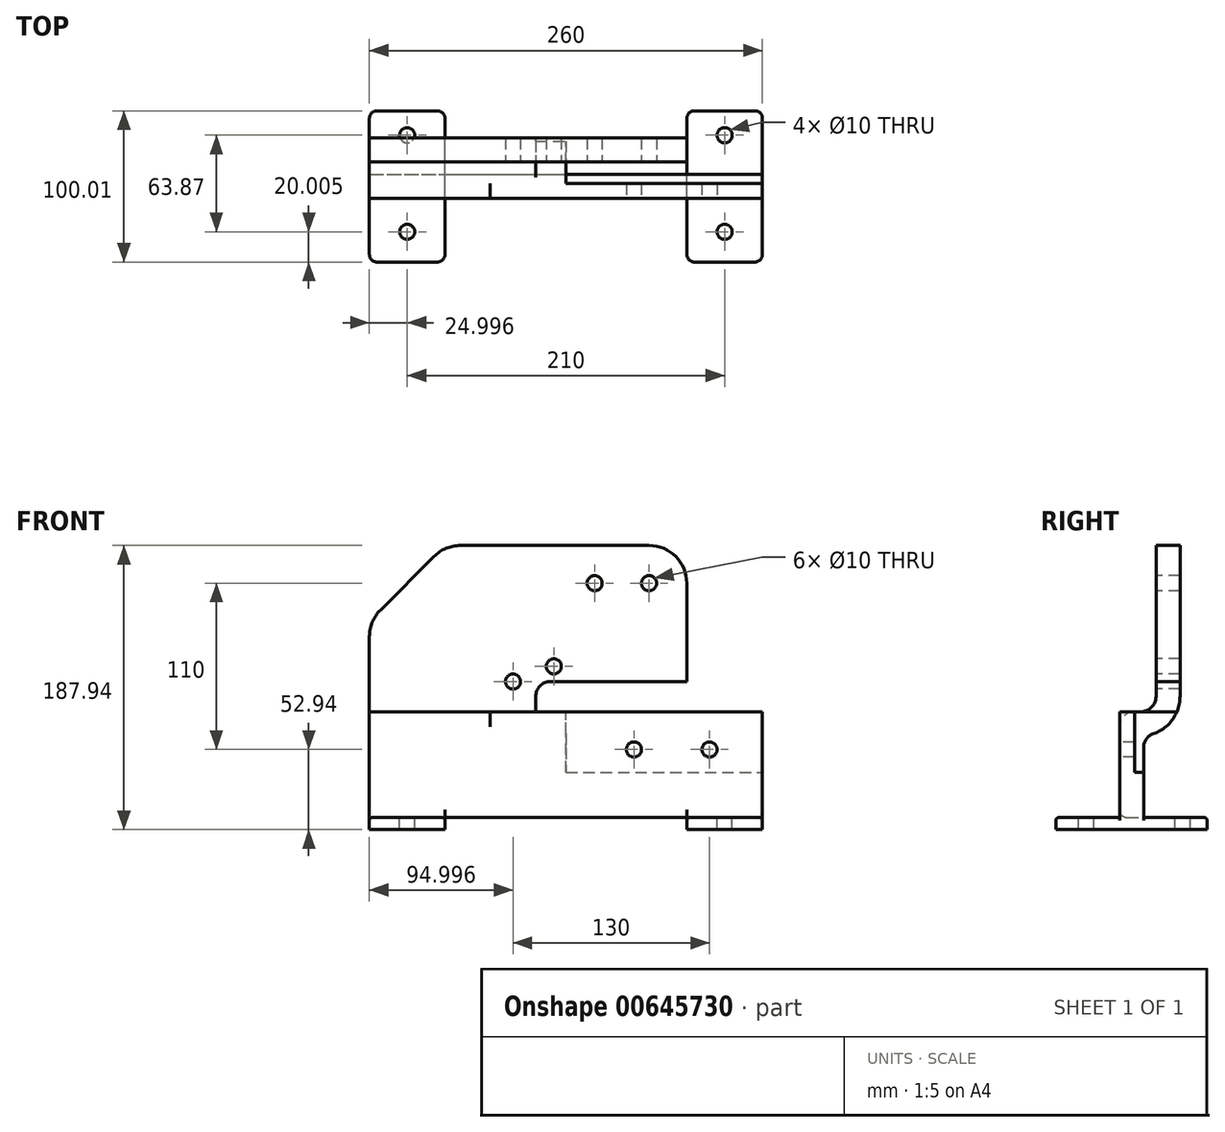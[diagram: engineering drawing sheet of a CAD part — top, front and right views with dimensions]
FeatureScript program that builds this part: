
annotation { "Feature Type Name" : "Feature", "Feature Type Description" : "" }
export const myFeature = defineFeature(function(context is Context, id is Id, definition is map)
    precondition{}
    {
        {
            var Q0;
            Q0=qCreatedBy(makeId("Front.planeOp"),FACE);
            var sketch = newSketch(context, id + "F0", { "sketchPlane" : qUnion([Q0])});
            skLineSegment(sketch, "E0", {"start": v(-123.11, 0) * mm, "end": v(136.89, 0) * mm});
            skLineSegment(sketch, "E1", {"start": v(136.89, 0) * mm, "end": v(136.89, 70) * mm});
            skLineSegment(sketch, "E2", {"start": v(136.89, 70) * mm, "end": v(-13.11, 70) * mm});
            skLineSegment(sketch, "E3", {"start": v(-13.11, 70) * mm, "end": v(-13.11, 80) * mm});
            skLineSegment(sketch, "E4", {"start": v(-3.11, 90) * mm, "end": v(86.89, 90) * mm});
            skLineSegment(sketch, "E5", {"start": v(86.89, 90) * mm, "end": v(86.89, 155) * mm});
            skLineSegment(sketch, "E6", {"start": v(61.89, 180) * mm, "end": v(-62.76, 180) * mm});
            skLineSegment(sketch, "E7", {"start": v(-80.44, 172.68) * mm, "end": v(-115.8, 137.32) * mm});
            skLineSegment(sketch, "E8", {"start": v(-123.11, 119.64) * mm, "end": v(-123.11, 0) * mm});
            skPoint(sketch, "E9.visualSharp", {"position": v(86.89, 180) * mm});
            skArc(sketch, "E9.filletArc", {"start": v(86.89, 155) * mm, "mid": v(79.56, 172.68) * mm, "end": v(61.89, 180) * mm});
            skPoint(sketch, "E10.visualSharp", {"position": v(-73.11, 180) * mm});
            skArc(sketch, "E10.filletArc", {"start": v(-62.76, 180) * mm, "mid": v(-72.33, 178.1) * mm, "end": v(-80.44, 172.68) * mm});
            skPoint(sketch, "E11.visualSharp", {"position": v(-123.11, 130) * mm});
            skArc(sketch, "E11.filletArc", {"start": v(-115.8, 137.32) * mm, "mid": v(-121.21, 129.21) * mm, "end": v(-123.11, 119.64) * mm});
            skPoint(sketch, "E12.visualSharp", {"position": v(-13.11, 90) * mm});
            skArc(sketch, "E12.filletArc", {"start": v(-3.11, 90) * mm, "mid": v(-10.18, 87.07) * mm, "end": v(-13.11, 80) * mm});
            skSolve(sketch);
        }
        {
            var Q0;
            Q0=makeQuery(id+"F0.imprint","IMPRINT",FACE,{"disambiguationData":[TD([[makeQuery(id+"F0.imprint","IMPRINT",EDGE,{"derivedFrom":sQuery(id+"F0.wireOp",EDGE,"E0")}),1.0]])]});
            extrude(context, id + "F1", {"entities" : qUnion([Q0]), "oppositeDirection" : true, "depth" : 40 * mm, "offsetDistance" : 25 * mm});
        }
        {
            var Q0;
            Q0=makeQuery(id+"F1.opExtrude","SWEPT_FACE",FACE,{"disambiguationData":[OSD([sQuery(id+"F0.wireOp",EDGE,"E1")])]});
            var sketch = newSketch(context, id + "F2", { "sketchPlane" : qUnion([Q0])});
            skLineSegment(sketch, "E13", {"start": v(15.87, 0) * mm, "end": v(15.87, 46.1) * mm});
            skPoint(sketch, "E14.visualSharp", {"position": v(15.87, 70) * mm});
            skArc(sketch, "E14.filletArc", {"start": v(22.6, 55.55) * mm, "mid": v(17.72, 51.9) * mm, "end": v(15.87, 46.1) * mm});
            skArc(sketch, "E15", {"start": v(22.6, 55.55) * mm, "mid": v(35.2, 65) * mm, "end": v(40, 80) * mm});
            skLineSegment(sketch, "E16.0", {"start": v(40, 90) * mm, "end": v(40, 80) * mm});
            skPoint(sketch, "E17.orphan", {"position": v(40, 80) * mm});
            skLineSegment(sketch, "E18", {"start": v(15.87, 0) * mm, "end": v(40, 0) * mm});
            skLineSegment(sketch, "E19", {"start": v(40, 0) * mm, "end": v(40, 80) * mm});
            skSolve(sketch);
        }
        {
            var Q0;
            Q0 = qSketchRegion(id + "F2", true);
            extrude(context, id + "F3", {"entities" : qUnion([Q0]), "operationType" : NewBodyOperationType.REMOVE, "endBound" : BoundingType.THROUGH_ALL, "oppositeDirection" : true, "depth" : 25 * mm, "offsetDistance" : 25 * mm});
        }
        {
            var Q0;
            Q0=makeQuery(id+"F1.opExtrude","SWEPT_FACE",FACE,{"disambiguationData":[OSD([sQuery(id+"F0.wireOp",EDGE,"E5")])]});
            var sketch = newSketch(context, id + "F4", { "sketchPlane" : qUnion([Q0])});
            skLineSegment(sketch, "E20", {"start": v(0, 70) * mm, "end": v(24.13, 70) * mm});
            skLineSegment(sketch, "E21", {"start": v(24.13, 180) * mm, "end": v(24.13, 70) * mm});
            skPoint(sketch, "E21.endSnap0", {"position": v(20, 90) * mm});
            skLineSegment(sketch, "E22", {"start": v(24.13, 180) * mm, "end": v(0, 180) * mm});
            skLineSegment(sketch, "E23", {"start": v(0, 180) * mm, "end": v(0, 70) * mm});
            skSolve(sketch);
        }
        {
            var Q0;
            Q0 = qSketchRegion(id + "F4", true);
            extrude(context, id + "F5", {"entities" : qUnion([Q0]), "operationType" : NewBodyOperationType.REMOVE, "oppositeDirection" : true, "depth" : 402 * mm, "offsetDistance" : 25 * mm});
        }
        {
            var Q0;
            Q0=makeQuery(id+"F5.boolean.opBoolean","COPY",EDGE,{"derivedFrom":makeQuery(id+"F5.opExtrude","SWEPT_EDGE",EDGE,{"disambiguationData":[OSD([sQuery(id+"F4.wireOp",EDGE,"E20"),sQuery(id+"F4.wireOp",EDGE,"E21")])]})});
            fillet(context, id + "F6", {"entities" : qUnion([Q0]), "radius" : 10 * mm, "tangentPropagation" : true, "allowEdgeOverflow" : false});
        }
        {
            var Q0;
            Q0=makeQuery(id+"F3.boolean.opBoolean","COPY",FACE,{"derivedFrom":makeQuery(id+"F3.opExtrude","SWEPT_FACE",FACE,{"disambiguationData":[OSD([sQuery(id+"F2.wireOp",EDGE,"E13")])]})});
            cPlane(context, id + "F7", {"entities" : qUnion([Q0]), "cplaneType" : CPlaneType.OFFSET, "offset" : 6 * mm, "oppositeDirection" : true, "width" : 150 * mm, "height" : 150 * mm});
        }
        {
            var Q0;
            Q0=qCreatedBy(id+"F7.planeOp",FACE);
            var sketch = newSketch(context, id + "F8", { "sketchPlane" : qUnion([Q0])});
            skLineSegment(sketch, "E24", {"start": v(-136.89, 30) * mm, "end": v(-6.89, 30) * mm});
            skLineSegment(sketch, "E25", {"start": v(-6.89, 30) * mm, "end": v(-6.89, 70) * mm});
            skLineSegment(sketch, "E26", {"start": v(-6.89, 70) * mm, "end": v(-136.89, 70) * mm});
            skLineSegment(sketch, "E27", {"start": v(-136.89, 70) * mm, "end": v(-136.89, 30) * mm});
            skSolve(sketch);
        }
        {
            var Q0;
            Q0 = qSketchRegion(id + "F8", true);
            extrude(context, id + "F9", {"entities" : qUnion([Q0]), "operationType" : NewBodyOperationType.REMOVE, "depth" : 30 * mm, "offsetDistance" : 25 * mm});
        }
        {
            var Q0;
            Q0=makeQuery(id+"F1.opExtrude","SWEPT_FACE",FACE,{"disambiguationData":[OSD([sQuery(id+"F0.wireOp",EDGE,"E8")])]});
            var sketch = newSketch(context, id + "F10", { "sketchPlane" : qUnion([Q0])});
            skArc(sketch, "E28", {"start": v(0, 60.16) * mm, "mid": v(-2.88, 67.12) * mm, "end": v(-9.84, 70) * mm});
            skLineSegment(sketch, "E29", {"start": v(-9.84, 70) * mm, "end": v(0, 70) * mm});
            skLineSegment(sketch, "E30", {"start": v(0, 70) * mm, "end": v(0, 60.16) * mm});
            skSolve(sketch);
        }
        {
            var Q0;
            Q0=makeQuery(id+"F10.imprint","IMPRINT",FACE,{"disambiguationData":[TD([[makeQuery(id+"F10.imprint","IMPRINT",EDGE,{"derivedFrom":sQuery(id+"F10.wireOp",EDGE,"E28")}),-1.0]])]});
            extrude(context, id + "F11", {"entities" : qUnion([Q0]), "operationType" : NewBodyOperationType.REMOVE, "oppositeDirection" : true, "depth" : 80 * mm, "offsetDistance" : 25 * mm});
        }
        {
            var Q0;
            Q0=makeQuery(id+"F1.opExtrude","SWEPT_FACE",FACE,{"disambiguationData":[OSD([sQuery(id+"F0.wireOp",EDGE,"E0")])]});
            var sketch = newSketch(context, id + "F12", { "sketchPlane" : qUnion([Q0])});
            skLineSegment(sketch, "E31.bottom", {"start": v(136.89, 42.07) * mm, "end": v(86.89, 42.07) * mm});
            skLineSegment(sketch, "E31.top", {"start": v(136.89, -57.94) * mm, "end": v(86.89, -57.94) * mm});
            skLineSegment(sketch, "E31.left", {"start": v(136.89, 42.07) * mm, "end": v(136.89, -57.94) * mm});
            skLineSegment(sketch, "E31.right", {"start": v(86.89, 42.07) * mm, "end": v(86.89, -57.94) * mm});
            skLineSegment(sketch, "E32.bottom", {"start": v(-73.11, 42.07) * mm, "end": v(-123.11, 42.07) * mm});
            skLineSegment(sketch, "E32.top", {"start": v(-73.11, -57.94) * mm, "end": v(-123.11, -57.94) * mm});
            skLineSegment(sketch, "E32.left", {"start": v(-73.11, 42.07) * mm, "end": v(-73.11, -57.94) * mm});
            skLineSegment(sketch, "E32.right", {"start": v(-123.11, 42.07) * mm, "end": v(-123.11, -57.94) * mm});
            skLineSegment(sketch, "E33", {"start": v(-123.11, -7.93) * mm, "end": v(136.89, -7.93) * mm, "construction": true});
            skSolve(sketch);
        }
        {
            var Q0;
            Q0 = qSketchRegion(id + "F12", true);
            extrude(context, id + "F13", {"entities" : qUnion([Q0]), "operationType" : NewBodyOperationType.ADD, "depth" : 7.94 * mm, "offsetDistance" : 25 * mm});
        }
        {
            var Q0;
            {var subQ0=sQuery(id+"F12.wireOp",EDGE,"E32.bottom");var subQ3=sQuery(id+"F12.wireOp",EDGE,"E32.left");var subQ4=sQuery(id+"F12.wireOp",EDGE,"E32.right");Q0=makeQuery(id+"F13.boolean.opBoolean","SPLIT",FACE,{"disambiguationData":[TD([makeQuery(id+"F13.opExtrude","SWEPT_FACE",FACE,{"disambiguationData":[OSD([subQ0])]})])],"derivedFrom":makeQuery(id+"F13.opExtrude","CAP_FACE",FACE,{"disambiguationData":[OSD([subQ0,sQuery(id+"F12.wireOp",EDGE,"E32.top"),subQ3,subQ4])],"isStart":true})});}
            var sketch = newSketch(context, id + "F14", { "sketchPlane" : qUnion([Q0])});
            skCircle(sketch, "E34", {"center": v(-98.11, -22.07) * mm, "radius": 5 * mm});
            skPoint(sketch, "E34.centerSnap0", {"position": v(-98.11, -42.07) * mm});
            skCircle(sketch, "E35.MirrorC", {"center": v(-98.11, 41.8) * mm, "radius": 5 * mm});
            skCircle(sketch, "E36", {"center": v(111.89, 41.8) * mm, "radius": 5 * mm});
            skLineSegment(sketch, "E37.0", {"start": v(136.89, 57.94) * mm, "end": v(86.89, 57.94) * mm, "construction": true});
            skLineSegment(sketch, "E38", {"start": v(111.89, 57.94) * mm, "end": v(111.89, 53.39) * mm, "construction": true});
            skCircle(sketch, "E39.MirrorC", {"center": v(111.89, -22.07) * mm, "radius": 5 * mm});
            skSolve(sketch);
        }
        {
            var Q0;
            Q0 = qSketchRegion(id + "F14", true);
            extrude(context, id + "F15", {"entities" : qUnion([Q0]), "operationType" : NewBodyOperationType.REMOVE, "oppositeDirection" : true, "depth" : 25 * mm, "offsetDistance" : 25 * mm});
        }
        {
            var Q0;
            Q0=makeQuery(id+"F1.opExtrude","CAP_FACE",FACE,{"disambiguationData":[OSD([sQuery(id+"F0.wireOp",EDGE,"E0"),sQuery(id+"F0.wireOp",EDGE,"E1"),sQuery(id+"F0.wireOp",EDGE,"E2"),sQuery(id+"F0.wireOp",EDGE,"E3"),sQuery(id+"F0.wireOp",EDGE,"E4"),sQuery(id+"F0.wireOp",EDGE,"E5"),sQuery(id+"F0.wireOp",EDGE,"E6"),sQuery(id+"F0.wireOp",EDGE,"E7"),sQuery(id+"F0.wireOp",EDGE,"E8"),sQuery(id+"F0.wireOp",EDGE,"E9.filletArc"),sQuery(id+"F0.wireOp",EDGE,"E10.filletArc"),sQuery(id+"F0.wireOp",EDGE,"E11.filletArc"),sQuery(id+"F0.wireOp",EDGE,"E12.filletArc")])],"isStart":true});
            var sketch = newSketch(context, id + "F16", { "sketchPlane" : qUnion([Q0])});
            skCircle(sketch, "E40", {"center": v(61.89, 155) * mm, "radius": 5 * mm});
            skCircle(sketch, "E41", {"center": v(25.89, 155) * mm, "radius": 5 * mm});
            skCircle(sketch, "E42", {"center": v(-1.11, 100) * mm, "radius": 5 * mm});
            skCircle(sketch, "E43", {"center": v(-28.11, 90) * mm, "radius": 5 * mm});
            skCircle(sketch, "E44", {"center": v(101.89, 45) * mm, "radius": 5 * mm});
            skCircle(sketch, "E45", {"center": v(51.89, 45) * mm, "radius": 5 * mm});
            skArc(sketch, "E46.0", {"start": v(61.89, 180) * mm, "mid": v(79.56, 172.68) * mm, "end": v(86.89, 155) * mm});
            skSolve(sketch);
        }
        {
            var Q0;
            Q0 = qSketchRegion(id + "F16", true);
            extrude(context, id + "F17", {"entities" : qUnion([Q0]), "operationType" : NewBodyOperationType.REMOVE, "endBound" : BoundingType.THROUGH_ALL, "oppositeDirection" : true, "depth" : 25 * mm, "offsetDistance" : 25 * mm});
        }
        {
            var Q0;
            {var subQ0=sQuery(id+"F0.wireOp",EDGE,"E0");Q0=makeQuery(id+"F13.boolean.opBoolean","SPLIT",EDGE,{"disambiguationData":[topologyDisambiguationEdgeConnected([makeQuery(id+"F13.opExtrude","CAP_FACE",FACE,{"disambiguationData":[OSD([sQuery(id+"F12.wireOp",EDGE,"E32.bottom"),sQuery(id+"F12.wireOp",EDGE,"E32.top"),sQuery(id+"F12.wireOp",EDGE,"E32.left"),sQuery(id+"F12.wireOp",EDGE,"E32.right")])],"isStart":true})])],"derivedFrom":makeQuery(id+"F1.opExtrude","CAP_EDGE",EDGE,{"disambiguationData":[OSD([subQ0])],"isStart":true})});}
            var Q1;
            {var subQ0=sQuery(id+"F0.wireOp",EDGE,"E0");Q1=makeQuery(id+"F13.boolean.opBoolean","SPLIT",EDGE,{"disambiguationData":[topologyDisambiguationEdgeConnected([makeQuery(id+"F13.opExtrude","CAP_FACE",FACE,{"disambiguationData":[OSD([sQuery(id+"F12.wireOp",EDGE,"E31.bottom"),sQuery(id+"F12.wireOp",EDGE,"E31.top"),sQuery(id+"F12.wireOp",EDGE,"E31.left"),sQuery(id+"F12.wireOp",EDGE,"E31.right")])],"isStart":true})])],"derivedFrom":makeQuery(id+"F1.opExtrude","CAP_EDGE",EDGE,{"disambiguationData":[OSD([subQ0])],"isStart":true})});}
            var Q2;
            {var subQ0=sQuery(id+"F2.wireOp",EDGE,"E13");Q2=makeQuery(id+"F13.boolean.opBoolean","SPLIT",EDGE,{"disambiguationData":[topologyDisambiguationEdgeConnected([makeQuery(id+"F13.opExtrude","CAP_FACE",FACE,{"disambiguationData":[OSD([sQuery(id+"F12.wireOp",EDGE,"E31.bottom"),sQuery(id+"F12.wireOp",EDGE,"E31.top"),sQuery(id+"F12.wireOp",EDGE,"E31.left"),sQuery(id+"F12.wireOp",EDGE,"E31.right")])],"isStart":true})])],"derivedFrom":makeQuery(id+"F3.boolean.opBoolean","COPY",EDGE,{"derivedFrom":makeQuery(id+"F3.opExtrude","SWEPT_EDGE",EDGE,{"disambiguationData":[OSD([sQuery(id+"F0.wireOp",EDGE,"E0"),sQuery(id+"F0.wireOp",EDGE,"E1"),subQ0,sQuery(id+"F2.wireOp",EDGE,"E18")])]})})});}
            var Q3;
            {var subQ0=sQuery(id+"F2.wireOp",EDGE,"E13");Q3=makeQuery(id+"F13.boolean.opBoolean","SPLIT",EDGE,{"disambiguationData":[topologyDisambiguationEdgeConnected([makeQuery(id+"F13.opExtrude","CAP_FACE",FACE,{"disambiguationData":[OSD([sQuery(id+"F12.wireOp",EDGE,"E32.bottom"),sQuery(id+"F12.wireOp",EDGE,"E32.top"),sQuery(id+"F12.wireOp",EDGE,"E32.left"),sQuery(id+"F12.wireOp",EDGE,"E32.right")])],"isStart":true})])],"derivedFrom":makeQuery(id+"F3.boolean.opBoolean","COPY",EDGE,{"derivedFrom":makeQuery(id+"F3.opExtrude","SWEPT_EDGE",EDGE,{"disambiguationData":[OSD([sQuery(id+"F0.wireOp",EDGE,"E0"),sQuery(id+"F0.wireOp",EDGE,"E1"),subQ0,sQuery(id+"F2.wireOp",EDGE,"E18")])]})})});}
            fillet(context, id + "F18", {"entities" : qUnion([Q0, Q1, Q2, Q3]), "radius" : 5 * mm, "tangentPropagation" : true, "allowEdgeOverflow" : false});
        }
        {
            var Q0;
            Q0=makeQuery(id+"F13.opExtrude","SWEPT_EDGE",EDGE,{"disambiguationData":[OSD([sQuery(id+"F12.wireOp",EDGE,"E31.bottom"),sQuery(id+"F12.wireOp",EDGE,"E31.left")])]});
            var Q1;
            Q1=makeQuery(id+"F13.opExtrude","SWEPT_EDGE",EDGE,{"disambiguationData":[OSD([sQuery(id+"F12.wireOp",EDGE,"E31.top"),sQuery(id+"F12.wireOp",EDGE,"E31.left")])]});
            var Q2;
            Q2=makeQuery(id+"F13.opExtrude","SWEPT_EDGE",EDGE,{"disambiguationData":[OSD([sQuery(id+"F12.wireOp",EDGE,"E31.bottom"),sQuery(id+"F12.wireOp",EDGE,"E31.right")])]});
            var Q3;
            Q3=makeQuery(id+"F13.opExtrude","SWEPT_EDGE",EDGE,{"disambiguationData":[OSD([sQuery(id+"F12.wireOp",EDGE,"E31.top"),sQuery(id+"F12.wireOp",EDGE,"E31.right")])]});
            var Q4;
            Q4=makeQuery(id+"F13.opExtrude","SWEPT_EDGE",EDGE,{"disambiguationData":[OSD([sQuery(id+"F12.wireOp",EDGE,"E32.top"),sQuery(id+"F12.wireOp",EDGE,"E32.left")])]});
            var Q5;
            Q5=makeQuery(id+"F13.opExtrude","SWEPT_EDGE",EDGE,{"disambiguationData":[OSD([sQuery(id+"F12.wireOp",EDGE,"E32.top"),sQuery(id+"F12.wireOp",EDGE,"E32.right")])]});
            var Q6;
            Q6=makeQuery(id+"F13.opExtrude","SWEPT_EDGE",EDGE,{"disambiguationData":[OSD([sQuery(id+"F12.wireOp",EDGE,"E32.bottom"),sQuery(id+"F12.wireOp",EDGE,"E32.right")])]});
            var Q7;
            Q7=makeQuery(id+"F13.opExtrude","SWEPT_EDGE",EDGE,{"disambiguationData":[OSD([sQuery(id+"F12.wireOp",EDGE,"E32.bottom"),sQuery(id+"F12.wireOp",EDGE,"E32.left")])]});
            fillet(context, id + "F19", {"entities" : qUnion([Q0, Q1, Q2, Q3, Q4, Q5, Q6, Q7]), "radius" : 5 * mm, "tangentPropagation" : true, "allowEdgeOverflow" : false});
        }
        {
            var Q0;
            {var subQ0=sQuery(id+"F12.wireOp",EDGE,"E32.bottom");var subQ3=sQuery(id+"F12.wireOp",EDGE,"E32.left");var subQ4=sQuery(id+"F12.wireOp",EDGE,"E32.right");Q0=makeQuery(id+"F19.opFillet","BLEND_EDGE",EDGE,{"blendedFrom":[makeQuery(id+"F13.opExtrude","SWEPT_EDGE",EDGE,{"disambiguationData":[OSD([subQ0,subQ3])]}),makeQuery(id+"F13.boolean.opBoolean","SPLIT",FACE,{"disambiguationData":[TD([makeQuery(id+"F13.opExtrude","SWEPT_FACE",FACE,{"disambiguationData":[OSD([subQ0])]})])],"derivedFrom":makeQuery(id+"F13.opExtrude","CAP_FACE",FACE,{"disambiguationData":[OSD([subQ0,sQuery(id+"F12.wireOp",EDGE,"E32.top"),subQ3,subQ4])],"isStart":true})})],"blendedInto":[makeQuery(id+"F13.boolean.opBoolean","SPLIT",FACE,{"disambiguationData":[TD([makeQuery(id+"F13.opExtrude","SWEPT_FACE",FACE,{"disambiguationData":[OSD([subQ0])]})])],"derivedFrom":makeQuery(id+"F13.opExtrude","CAP_FACE",FACE,{"disambiguationData":[OSD([subQ0,sQuery(id+"F12.wireOp",EDGE,"E32.top"),subQ3,subQ4])],"isStart":true})})]});}
            var Q1;
            {var subQ0=sQuery(id+"F12.wireOp",EDGE,"E32.top");var subQ1=sQuery(id+"F12.wireOp",EDGE,"E32.left");var subQ2=sQuery(id+"F12.wireOp",EDGE,"E32.right");Q1=makeQuery(id+"F19.opFillet","BLEND_EDGE",EDGE,{"blendedFrom":[makeQuery(id+"F13.opExtrude","SWEPT_EDGE",EDGE,{"disambiguationData":[OSD([subQ0,subQ1])]}),makeQuery(id+"F13.boolean.opBoolean","SPLIT",FACE,{"disambiguationData":[TD([makeQuery(id+"F3.boolean.opBoolean","COPY",FACE,{"derivedFrom":makeQuery(id+"F3.opExtrude","SWEPT_FACE",FACE,{"disambiguationData":[OSD([sQuery(id+"F2.wireOp",EDGE,"E13")])]})})])],"derivedFrom":makeQuery(id+"F13.opExtrude","CAP_FACE",FACE,{"disambiguationData":[OSD([sQuery(id+"F12.wireOp",EDGE,"E32.bottom"),subQ0,subQ1,subQ2])],"isStart":true})})],"blendedInto":[makeQuery(id+"F13.boolean.opBoolean","SPLIT",FACE,{"disambiguationData":[TD([makeQuery(id+"F3.boolean.opBoolean","COPY",FACE,{"derivedFrom":makeQuery(id+"F3.opExtrude","SWEPT_FACE",FACE,{"disambiguationData":[OSD([sQuery(id+"F2.wireOp",EDGE,"E13")])]})})])],"derivedFrom":makeQuery(id+"F13.opExtrude","CAP_FACE",FACE,{"disambiguationData":[OSD([sQuery(id+"F12.wireOp",EDGE,"E32.bottom"),subQ0,subQ1,subQ2])],"isStart":true})})]});}
            var Q2;
            {var subQ0=sQuery(id+"F12.wireOp",EDGE,"E31.right");var subQ1=sQuery(id+"F12.wireOp",EDGE,"E31.top");var subQ2=sQuery(id+"F12.wireOp",EDGE,"E31.left");Q2=makeQuery(id+"F19.opFillet","BLEND_EDGE",EDGE,{"blendedFrom":[makeQuery(id+"F13.opExtrude","SWEPT_EDGE",EDGE,{"disambiguationData":[OSD([subQ1,subQ0])]}),makeQuery(id+"F13.boolean.opBoolean","SPLIT",FACE,{"disambiguationData":[TD([makeQuery(id+"F3.boolean.opBoolean","COPY",FACE,{"derivedFrom":makeQuery(id+"F3.opExtrude","SWEPT_FACE",FACE,{"disambiguationData":[OSD([sQuery(id+"F2.wireOp",EDGE,"E13")])]})})])],"derivedFrom":makeQuery(id+"F13.opExtrude","CAP_FACE",FACE,{"disambiguationData":[OSD([sQuery(id+"F12.wireOp",EDGE,"E31.bottom"),subQ1,subQ2,subQ0])],"isStart":true})})],"blendedInto":[makeQuery(id+"F13.boolean.opBoolean","SPLIT",FACE,{"disambiguationData":[TD([makeQuery(id+"F3.boolean.opBoolean","COPY",FACE,{"derivedFrom":makeQuery(id+"F3.opExtrude","SWEPT_FACE",FACE,{"disambiguationData":[OSD([sQuery(id+"F2.wireOp",EDGE,"E13")])]})})])],"derivedFrom":makeQuery(id+"F13.opExtrude","CAP_FACE",FACE,{"disambiguationData":[OSD([sQuery(id+"F12.wireOp",EDGE,"E31.bottom"),subQ1,subQ2,subQ0])],"isStart":true})})]});}
            var Q3;
            {var subQ0=sQuery(id+"F12.wireOp",EDGE,"E31.bottom");var subQ3=sQuery(id+"F12.wireOp",EDGE,"E31.left");var subQ4=sQuery(id+"F12.wireOp",EDGE,"E31.right");Q3=makeQuery(id+"F19.opFillet","BLEND_EDGE",EDGE,{"blendedFrom":[makeQuery(id+"F13.opExtrude","SWEPT_EDGE",EDGE,{"disambiguationData":[OSD([subQ0,subQ3])]}),makeQuery(id+"F13.boolean.opBoolean","SPLIT",FACE,{"disambiguationData":[TD([makeQuery(id+"F13.opExtrude","SWEPT_FACE",FACE,{"disambiguationData":[OSD([subQ0])]})])],"derivedFrom":makeQuery(id+"F13.opExtrude","CAP_FACE",FACE,{"disambiguationData":[OSD([subQ0,sQuery(id+"F12.wireOp",EDGE,"E31.top"),subQ3,subQ4])],"isStart":true})})],"blendedInto":[makeQuery(id+"F13.boolean.opBoolean","SPLIT",FACE,{"disambiguationData":[TD([makeQuery(id+"F13.opExtrude","SWEPT_FACE",FACE,{"disambiguationData":[OSD([subQ0])]})])],"derivedFrom":makeQuery(id+"F13.opExtrude","CAP_FACE",FACE,{"disambiguationData":[OSD([subQ0,sQuery(id+"F12.wireOp",EDGE,"E31.top"),subQ3,subQ4])],"isStart":true})})]});}
            fillet(context, id + "F20", {"entities" : qUnion([Q0, Q1, Q2, Q3]), "radius" : 2 * mm, "tangentPropagation" : true, "allowEdgeOverflow" : false});
        }
    });
